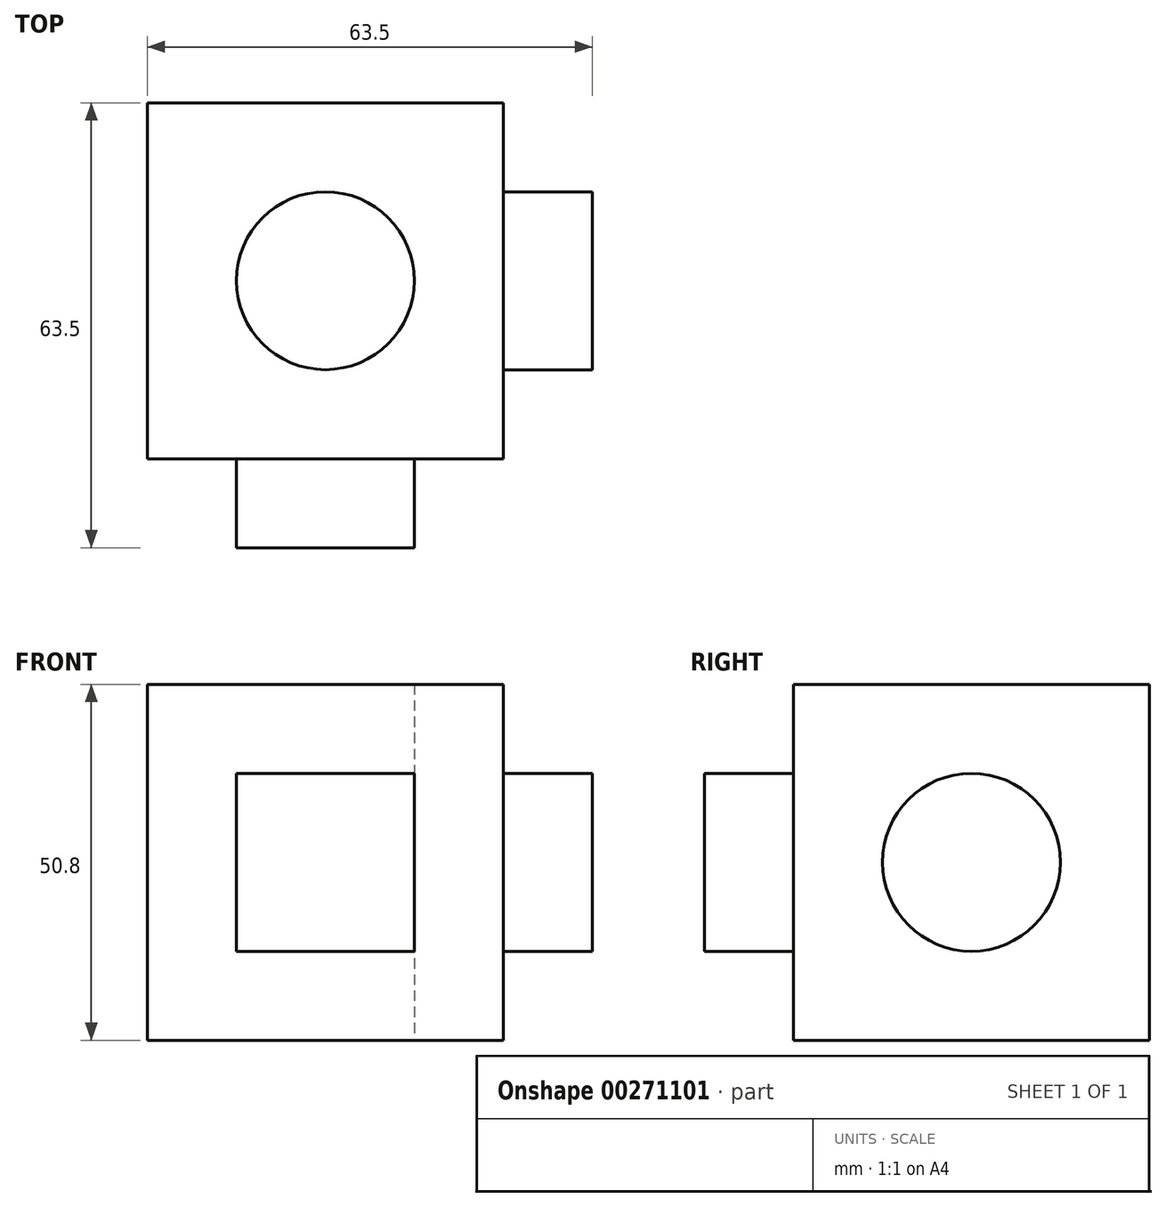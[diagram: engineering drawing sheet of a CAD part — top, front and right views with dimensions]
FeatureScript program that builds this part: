
annotation { "Feature Type Name" : "Feature", "Feature Type Description" : "" }
export const myFeature = defineFeature(function(context is Context, id is Id, definition is map)
    precondition{}
    {
        {
            var Q0;
            Q0=qCreatedBy(makeId("Front.planeOp"),FACE);
            var sketch = newSketch(context, id + "F0", { "sketchPlane" : qUnion([Q0])});
            skLineSegment(sketch, "E0.bottom", {"start": v(0, 0) * mm, "end": v(50.8, 0) * mm});
            skLineSegment(sketch, "E0.top", {"start": v(0, 50.8) * mm, "end": v(50.8, 50.8) * mm});
            skLineSegment(sketch, "E0.left", {"start": v(0, 0) * mm, "end": v(0, 50.8) * mm});
            skLineSegment(sketch, "E0.right", {"start": v(50.8, 0) * mm, "end": v(50.8, 50.8) * mm});
            skSolve(sketch);
        }
        {
            var Q0;
            Q0=makeQuery(id+"F0.imprint","IMPRINT",FACE,{"disambiguationData":[TD([[makeQuery(id+"F0.imprint","IMPRINT",EDGE,{"derivedFrom":sQuery(id+"F0.wireOp",EDGE,"E0.bottom")}),1.0]])]});
            extrude(context, id + "F1", {"entities" : qUnion([Q0]), "depth" : 50.8 * mm});
        }
        {
            var Q0;
            Q0=makeQuery(id+"F1.opExtrude","CAP_FACE",FACE,{"disambiguationData":[OSD([sQuery(id+"F0.wireOp",EDGE,"E0.bottom"),sQuery(id+"F0.wireOp",EDGE,"E0.top"),sQuery(id+"F0.wireOp",EDGE,"E0.left"),sQuery(id+"F0.wireOp",EDGE,"E0.right")])],"isStart":false});
            var sketch = newSketch(context, id + "F2", { "sketchPlane" : qUnion([Q0])});
            skLineSegment(sketch, "E1.bottom", {"start": v(12.7, 38.1) * mm, "end": v(38.1, 38.1) * mm});
            skLineSegment(sketch, "E1.top", {"start": v(12.7, 12.7) * mm, "end": v(38.1, 12.7) * mm});
            skLineSegment(sketch, "E1.left", {"start": v(12.7, 38.1) * mm, "end": v(12.7, 12.7) * mm});
            skLineSegment(sketch, "E1.right", {"start": v(38.1, 38.1) * mm, "end": v(38.1, 12.7) * mm});
            skSolve(sketch);
        }
        {
            var Q0;
            Q0=makeQuery(id+"F2.imprint","IMPRINT",FACE,{"disambiguationData":[TD([[makeQuery(id+"F2.imprint","IMPRINT",EDGE,{"derivedFrom":sQuery(id+"F2.wireOp",EDGE,"E1.bottom")}),-1.0]])]});
            extrude(context, id + "F3", {"entities" : qUnion([Q0]), "operationType" : NewBodyOperationType.ADD, "depth" : 12.7 * mm});
        }
        {
            var Q0;
            Q0=makeQuery(id+"F1.opExtrude","SWEPT_FACE",FACE,{"disambiguationData":[OSD([sQuery(id+"F0.wireOp",EDGE,"E0.right")])]});
            var sketch = newSketch(context, id + "F4", { "sketchPlane" : qUnion([Q0])});
            skCircle(sketch, "E2", {"center": v(-25.4, 25.4) * mm, "radius": 12.7 * mm});
            skSolve(sketch);
        }
        {
            var Q0;
            Q0=makeQuery(id+"F4.imprint","IMPRINT",FACE,{"disambiguationData":[TD([[makeQuery(id+"F4.imprint","IMPRINT",EDGE,{"derivedFrom":sQuery(id+"F4.wireOp",EDGE,"E2")}),1.0]])]});
            extrude(context, id + "F5", {"entities" : qUnion([Q0]), "operationType" : NewBodyOperationType.ADD, "depth" : 12.7 * mm});
        }
        {
            var Q0;
            Q0=qCreatedBy(makeId("Top.planeOp"),FACE);
            var sketch = newSketch(context, id + "F6", { "sketchPlane" : qUnion([Q0])});
            skCircle(sketch, "E3", {"center": v(25.4, -25.4) * mm, "radius": 12.7 * mm});
            skSolve(sketch);
        }
        {
            var Q0;
            Q0=makeQuery(id+"F6.imprint","IMPRINT",FACE,{"disambiguationData":[TD([[makeQuery(id+"F6.imprint","IMPRINT",EDGE,{"derivedFrom":sQuery(id+"F6.wireOp",EDGE,"E3")}),1.0]])]});
            var Q1;
            Q1=sQuery(id+"F6.wireOp",EDGE,"E3");
            extrude(context, id + "F7", {"entities" : qUnion([Q0]), "operationType" : NewBodyOperationType.REMOVE, "surfaceEntities" : qUnion([Q1]), "depth" : 50.8 * mm});
        }
    });
